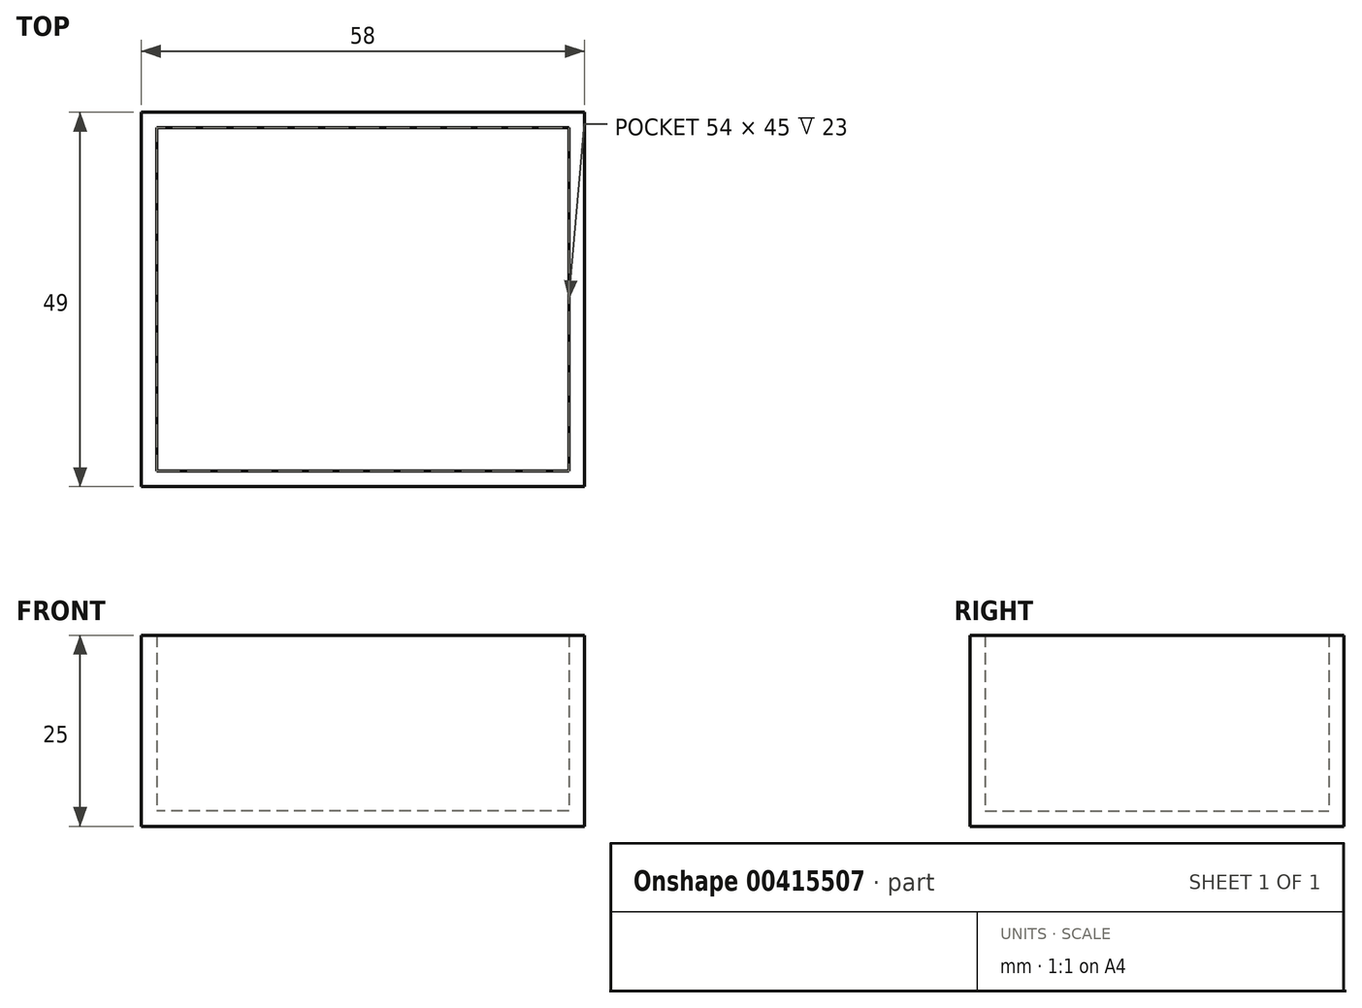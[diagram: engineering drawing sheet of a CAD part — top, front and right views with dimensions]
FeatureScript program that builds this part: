
annotation { "Feature Type Name" : "Feature", "Feature Type Description" : "" }
export const myFeature = defineFeature(function(context is Context, id is Id, definition is map)
    precondition{}
    {
        {
            var Q0;
            Q0=qCreatedBy(makeId("Top.planeOp"),FACE);
            var sketch = newSketch(context, id + "F0", { "sketchPlane" : qUnion([Q0])});
            skLineSegment(sketch, "E0.bottom", {"start": v(27, -22.5) * mm, "end": v(-27, -22.5) * mm});
            skLineSegment(sketch, "E0.top", {"start": v(27, 22.5) * mm, "end": v(-27, 22.5) * mm});
            skLineSegment(sketch, "E0.left", {"start": v(27, -22.5) * mm, "end": v(27, 22.5) * mm});
            skLineSegment(sketch, "E0.right", {"start": v(-27, -22.5) * mm, "end": v(-27, 22.5) * mm});
            skPoint(sketch, "E0.middle", {"position": v(0, 0) * mm});
            skLineSegment(sketch, "E1.bottom", {"start": v(0, -23.76) * mm, "end": v(-2.27, -23.76) * mm});
            skLineSegment(sketch, "E1.top", {"start": v(0, -23.76) * mm, "end": v(-2.27, -23.76) * mm});
            skLineSegment(sketch, "E1.left", {"start": v(0, -23.76) * mm, "end": v(0, -23.76) * mm});
            skLineSegment(sketch, "E1.right", {"start": v(-2.27, -23.76) * mm, "end": v(-2.27, -23.76) * mm});
            skPoint(sketch, "E1.middle", {"position": v(-1.13, -23.76) * mm});
            skLineSegment(sketch, "E2.0", {"start": v(29, 24.5) * mm, "end": v(-29, 24.5) * mm});
            skLineSegment(sketch, "E2.1", {"start": v(29, -24.5) * mm, "end": v(29, 24.5) * mm});
            skLineSegment(sketch, "E2.2", {"start": v(29, -24.5) * mm, "end": v(-29, -24.5) * mm});
            skLineSegment(sketch, "E2.3", {"start": v(-29, -24.5) * mm, "end": v(-29, 24.5) * mm});
            skSolve(sketch);
        }
        {
            var Q0;
            Q0=makeQuery(id+"F0.imprint","IMPRINT",FACE,{"disambiguationData":[TD([[makeQuery(id+"F0.imprint","IMPRINT",EDGE,{"derivedFrom":sQuery(id+"F0.wireOp",EDGE,"E0.bottom")}),-1.0]])]});
            extrude(context, id + "F1", {"entities" : qUnion([Q0]), "depth" : 2 * mm});
        }
        {
            var Q0;
            Q0 = qSketchRegion(id + "F0", true);
            extrude(context, id + "F2", {"entities" : qUnion([Q0]), "operationType" : NewBodyOperationType.ADD, "depth" : 25 * mm});
        }
    });
